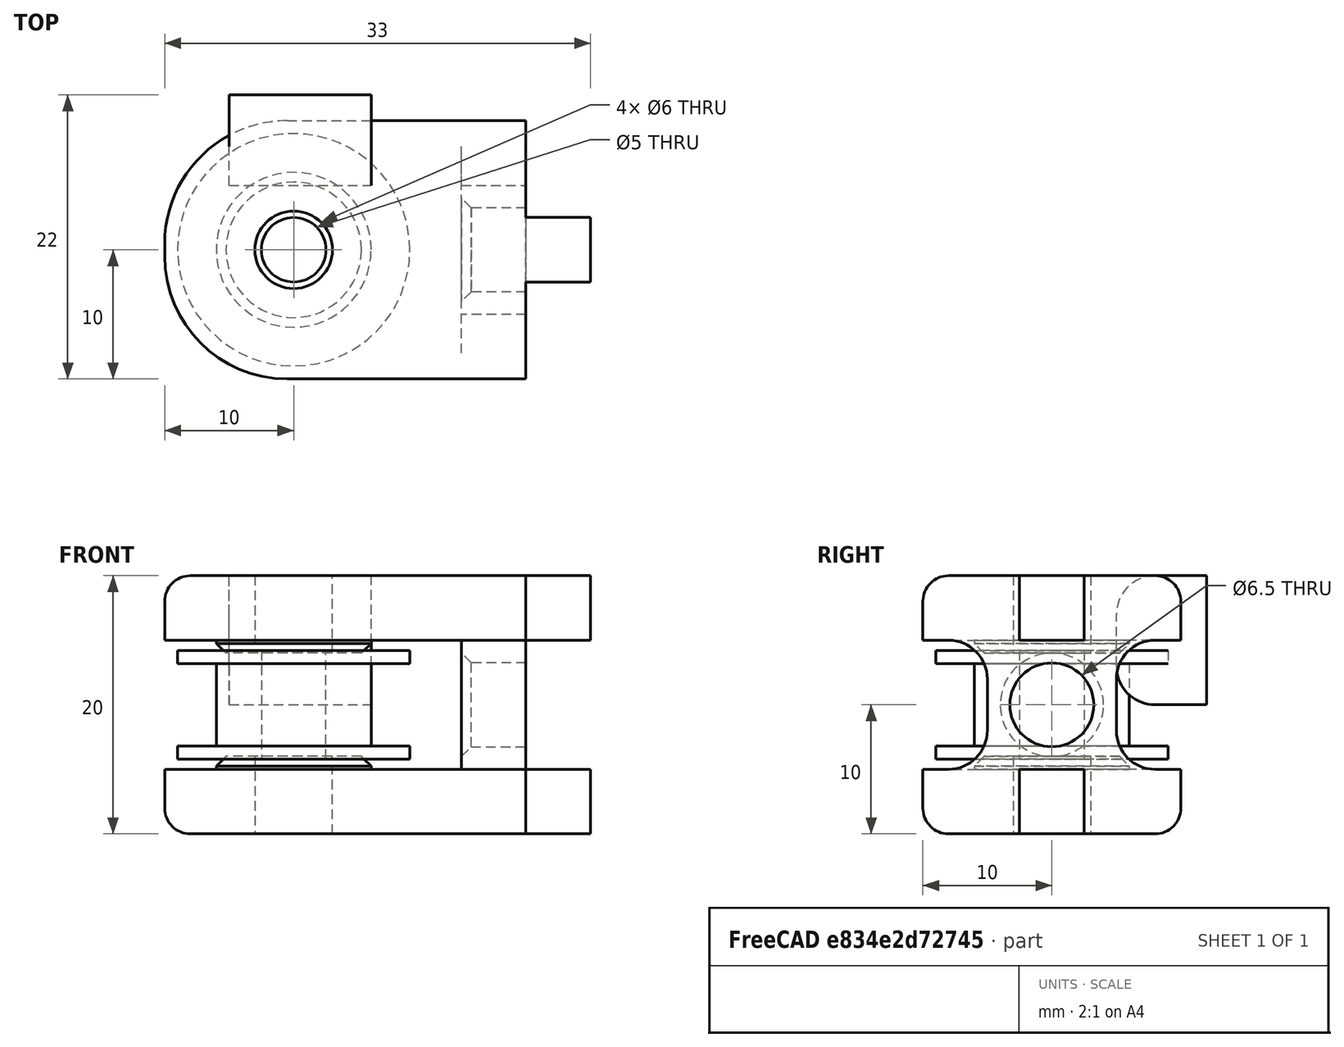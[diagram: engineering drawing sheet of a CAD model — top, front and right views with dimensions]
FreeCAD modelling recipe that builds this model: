
FCSTD DOCUMENT  (FreeCAD 0.20R29177 (Git))
Label: Pulley1
License: All rights reserved
LicenseURL: http://en.wikipedia.org/wiki/All_rights_reserved
objects: Part::Cylinder×8, Part::Box×6, Part::Cut×4, Part::MultiFuse×3, Part::Refine×3, PartDesign::FeatureBase×3, PartDesign::Fillet×3, PartDesign::Body×3, PartDesign::Chamfer×3, Part::Fuse×2, Part::FeaturePython×1
note: 44 computed .brp shape members not serialized (recipe doc carries the construction recipe); baked Part::Feature solids carry a one-line shape summary decoded from their .brp

FEATURE [Part::Cylinder] Cylinder  label="Cilindro"
  Angle = 360
  AttacherType = Attacher::AttachEngine3D
  FirstAngle = 0
  Height = 6.4
  Placement = pos=(0,0,-3.2) rot=(0,0,1;0rad)
  Radius = 6
  SecondAngle = 0
FEATURE [Part::Cylinder] Cylinder001  label="Cilindro001"
  Angle = 360
  AttacherType = Attacher::AttachEngine3D
  FirstAngle = 0
  Height = 1
  Placement = pos=(0,0,3.2) rot=(0,0,1;0rad)
  Radius = 9
  SecondAngle = 0
FEATURE [Part::Cylinder] Cylinder002  label="Cilindro002"
  Angle = 360
  AttacherType = Attacher::AttachEngine3D
  FirstAngle = 0
  Height = 1
  Placement = pos=(0,0,-4.2) rot=(0,0,1;0rad)
  Radius = 9
  SecondAngle = 0
FEATURE [Part::Fuse] Fusion
  Base = -> Cylinder
  Tool = -> Cylinder001
FEATURE [Part::Fuse] Fusion001
  Base = -> Cylinder002
  Tool = -> Fusion
FEATURE [Part::Cylinder] Cylinder003  label="Cilindro003"
  Angle = 360
  AttacherType = Attacher::AttachEngine3D
  FirstAngle = 0
  Height = 10
  Placement = pos=(0,0,-5) rot=(0,0,1;0rad)
  Radius = 2.5
  SecondAngle = 0
FEATURE [Part::Cut] Cut  label="Pulley"
  Base = -> Fusion001
  Tool = -> Cylinder003
FEATURE [Part::Box] Box  label="Base"
  AttacherType = Attacher::AttachEngine3D
  Height = 20
  Length = 5
  Placement = pos=(13,-10,-10) rot=(0,0,1;0rad)
  Width = 20
FEATURE [Part::Box] Box003  label="Cubo002"
  AttacherType = Attacher::AttachEngine3D
  Height = 5
  Length = 10
  Placement = pos=(13,-2.5,5) rot=(0,0,1;0rad)
  Width = 5
FEATURE [Part::Box] Box004  label="Cubo003"
  AttacherType = Attacher::AttachEngine3D
  Height = 5
  Length = 10
  Placement = pos=(13,-2.5,-10) rot=(0,0,1;0rad)
  Width = 5
FEATURE [Part::MultiFuse] Fusion002
  Shapes = -> [Box,Box003,Box004]
FEATURE [Part::Refine] Fusion002001
  Source = -> Fusion002
FEATURE [Part::Box] Box005  label="Cubo"
  AttacherType = Attacher::AttachEngine3D
  Height = 5
  Length = 23
  Placement = pos=(-10,-10,-10) rot=(-0.707107,0,0.707107;0rad)
  Width = 20
FEATURE [Part::Box] Box006  label="Cubo004"
  AttacherType = Attacher::AttachEngine3D
  Height = 5
  Length = 23
  Placement = pos=(-10,-10,5) rot=(-0.707107,0,0.707107;0rad)
  Width = 20
FEATURE [Part::MultiFuse] Fusion002002
  Shapes = -> [Box006,Box005,Fusion002001]
FEATURE [Part::Refine] Fusion002002001
  Source = -> Fusion002002
FEATURE [Part::Cylinder] Cylinder004  label="Cilindro004"
  Angle = 360
  AttacherType = Attacher::AttachEngine3D
  FirstAngle = 0
  Height = 30
  Placement = pos=(0,0,-15) rot=(0,0,1;0rad)
  Radius = 3
  SecondAngle = 0
FEATURE [Part::Cylinder] Cylinder005  label="apoyo2"
  Angle = 360
  AttacherType = Attacher::AttachEngine3D
  FirstAngle = 0
  Height = 4
  Placement = pos=(0,0,-8) rot=(0,0,1;0rad)
  Radius = 6
  SecondAngle = 0
FEATURE [Part::Cylinder] Cylinder006  label="apoyo1"
  Angle = 360
  AttacherType = Attacher::AttachEngine3D
  FirstAngle = 0
  Height = 4
  Placement = pos=(0,0,4) rot=(0,0,1;0rad)
  Radius = 6
  SecondAngle = 0
FEATURE [Part::MultiFuse] Fusion002002002
  Shapes = -> [Cylinder006,Cylinder005,Fusion002002001]
FEATURE [Part::Cut] Cut001
  Base = -> Fusion002002002
  Tool = -> Cylinder004
FEATURE [Part::Box] Box007  label="Cubo005"
  AttacherType = Attacher::AttachEngine3D
  Height = 10
  Length = 11
  Placement = pos=(10,5,-5) rot=(0,0,1;0rad)
  Width = 7
FEATURE [PartDesign::FeatureBase] BaseFeature
  BaseFeature = -> Box007
FEATURE [PartDesign::Fillet] Fillet
  Base = -> BaseFeature [Edge10,Edge9]
  BaseFeature = -> BaseFeature
  Radius = 3
  SupportTransform = false
  UseAllEdges = false
FEATURE [PartDesign::Body] Body
  BaseFeature = -> Box007
  Group = -> [BaseFeature,Fillet]
  Origin = -> Origin
  Placement = pos=(-5,5,0) rot=(0,0,1;0rad)
  Tip = -> Fillet
FEATURE [Part::FeaturePython] Array  # Draft array (typed FeaturePython)
  AlwaysSyncPlacement = false
  Angle = 180
  ArrayType = 1
  Axis = (0,0,1)
  Base = -> Body
  Center = (0,0,0)
  Count = 2
  ExpandArray = false
  Fuse = false
  IntervalAxis = (0,0,0)
  IntervalX = (50,0,0)
  IntervalY = (0,50,0)
  IntervalZ = (0,0,50)
  NumberCircles = 3
  NumberPolar = 2
  NumberX = 2
  NumberY = 2
  NumberZ = 1
  Placement = pos=(14,0,-5) rot=(0,0,1;0rad)
  PlacementList = 2 placements: [(-5,5,0),(5,-5,0)]
  RadialDistance = 50
  ScaleList = (2) [(1,1,1),(1,1,1)]
  Symmetry = 1
  TangentialDistance = 25
FEATURE [Part::Cut] Cut002
  Base = -> Cut001
  Tool = -> Array
FEATURE [Part::Refine] Cut002001
  Source = -> Cut002
FEATURE [PartDesign::FeatureBase] BaseFeature001
  BaseFeature = -> Cut002001
FEATURE [PartDesign::Chamfer] Chamfer
  Angle = 45
  Base = -> BaseFeature001 [Edge3]
  BaseFeature = -> BaseFeature001
  ChamferType = 0
  FlipDirection = false
  Size = 0.75
  Size2 = 1
  SupportTransform = false
  UseAllEdges = false
FEATURE [PartDesign::Chamfer] Chamfer001
  Angle = 45
  Base = -> Chamfer [Edge85]
  BaseFeature = -> Chamfer
  ChamferType = 0
  FlipDirection = false
  Size = 0.75
  Size2 = 1
  SupportTransform = false
  UseAllEdges = false
FEATURE [PartDesign::Fillet] Fillet001
  Base = -> Chamfer001 [Edge17,Edge48,Edge81,Edge68]
  BaseFeature = -> Chamfer001
  Radius = 9.5
  SupportTransform = false
  UseAllEdges = false
FEATURE [PartDesign::Fillet] Fillet002
  Base = -> Fillet001 [Edge14,Edge73]
  BaseFeature = -> Fillet001
  Radius = 2
  SupportTransform = false
  UseAllEdges = false
FEATURE [PartDesign::Body] Body001
  BaseFeature = -> Cut002001
  Group = -> [BaseFeature001,Chamfer,Chamfer001,Fillet001,Fillet002]
  Origin = -> Origin001
  Tip = -> Fillet002
FEATURE [Part::Cylinder] Cylinder007  label="Cilindro005"
  Angle = 360
  AttacherType = Attacher::AttachEngine3D
  FirstAngle = 0
  Height = 26
  Placement = pos=(0,0,0) rot=(0,1,0;1.5708rad)
  Radius = 3.25
  SecondAngle = 0
FEATURE [Part::Cut] Cut002002
  Base = -> Fillet002
  Tool = -> Cylinder007
FEATURE [PartDesign::FeatureBase] BaseFeature002
  BaseFeature = -> Cut002002
FEATURE [PartDesign::Chamfer] Chamfer002
  Angle = 45
  Base = -> BaseFeature002 [Edge66]
  BaseFeature = -> BaseFeature002
  ChamferType = 0
  FlipDirection = false
  Size = 0.75
  Size2 = 1
  SupportTransform = false
  UseAllEdges = false
FEATURE [PartDesign::Body] Body002
  BaseFeature = -> Cut002002
  Group = -> [BaseFeature002,Chamfer002]
  Origin = -> Origin002
  Tip = -> Chamfer002
